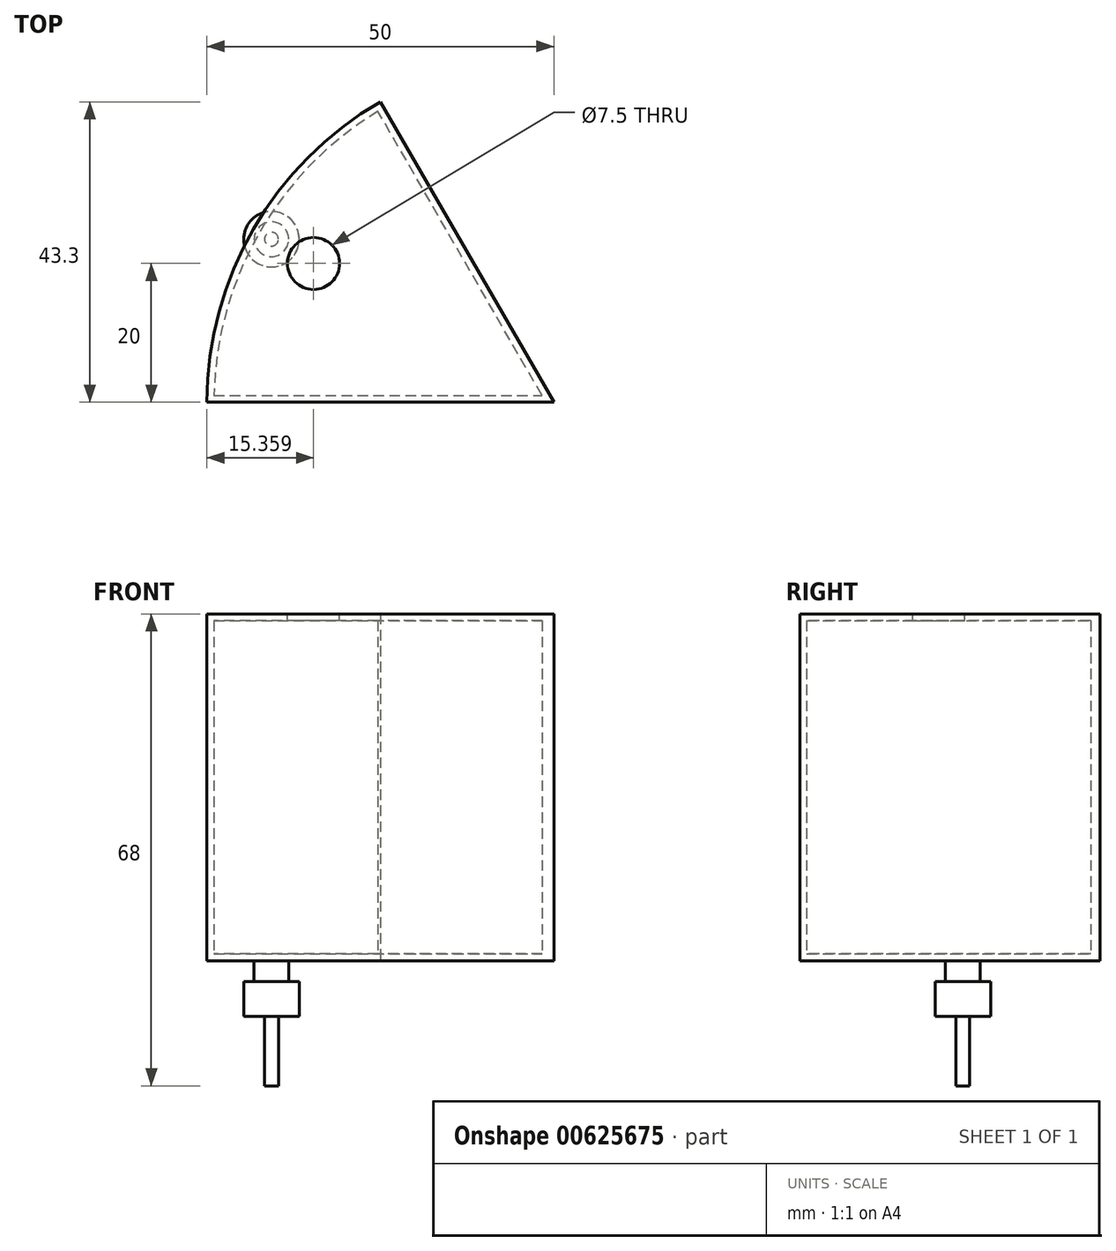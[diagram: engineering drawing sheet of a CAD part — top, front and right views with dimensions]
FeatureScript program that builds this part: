
annotation { "Feature Type Name" : "Feature", "Feature Type Description" : "" }
export const myFeature = defineFeature(function(context is Context, id is Id, definition is map)
    precondition{}
    {
        {
            var Q0;
            Q0=qCreatedBy(makeId("Top.planeOp"),FACE);
            var sketch = newSketch(context, id + "F0", { "sketchPlane" : qUnion([Q0])});
            skArc(sketch, "E0", {"start": v(-25, 43.3) * mm, "mid": v(-43.3, 25) * mm, "end": v(-50, 0) * mm});
            skLineSegment(sketch, "E1", {"start": v(-50, 0) * mm, "end": v(0, 0) * mm});
            skLineSegment(sketch, "E2", {"start": v(-25, 43.3) * mm, "end": v(0, 0) * mm});
            skSolve(sketch);
        }
        {
            var Q0;
            Q0=makeQuery(id+"F0.imprint","IMPRINT",FACE,{"disambiguationData":[TD([[makeQuery(id+"F0.imprint","IMPRINT",EDGE,{"derivedFrom":sQuery(id+"F0.wireOp",EDGE,"E0")}),1.0]])]});
            extrude(context, id + "F1", {"entities" : qUnion([Q0]), "depth" : 50 * mm, "offsetDistance" : 25 * mm});
        }
        {
            var Q0;
            Q0=qCreatedBy(makeId("Top.planeOp"),FACE);
            var sketch = newSketch(context, id + "F2", { "sketchPlane" : qUnion([Q0])});
            skArc(sketch, "E3", {"start": v(-25.36, 41.93) * mm, "mid": v(-42.44, 24.5) * mm, "end": v(-48.99, 1) * mm});
            skLineSegment(sketch, "E4", {"start": v(-48.99, 1) * mm, "end": v(-1.73, 1) * mm});
            skLineSegment(sketch, "E5", {"start": v(-1.73, 1) * mm, "end": v(-25.36, 41.93) * mm});
            skSolve(sketch);
        }
        {
            var Q0;
            Q0=makeQuery(id+"F2.imprint","IMPRINT",FACE,{"disambiguationData":[TD([[makeQuery(id+"F2.imprint","IMPRINT",EDGE,{"derivedFrom":sQuery(id+"F2.wireOp",EDGE,"E3")}),1.0]])]});
            extrude(context, id + "F3", {"entities" : qUnion([Q0]), "operationType" : NewBodyOperationType.REMOVE, "depth" : 49 * mm, "offsetDistance" : 25 * mm, "hasSecondDirection" : true, "secondDirectionOppositeDirection" : false, "secondDirectionDepth" : 1 * mm});
        }
        {
            var Q0;
            Q0=makeQuery(id+"F1.opExtrude","CAP_FACE",FACE,{"disambiguationData":[OSD([sQuery(id+"F0.wireOp",EDGE,"E0"),sQuery(id+"F0.wireOp",EDGE,"E1"),sQuery(id+"F0.wireOp",EDGE,"E2")])],"isStart":true});
            var sketch = newSketch(context, id + "F4", { "sketchPlane" : qUnion([Q0])});
            skCircle(sketch, "E6", {"center": v(-40.7, -23.5) * mm, "radius": 2.5 * mm});
            skSolve(sketch);
        }
        {
            var Q0;
            Q0=makeQuery(id+"F4.imprint","IMPRINT",FACE,{"disambiguationData":[TD([[makeQuery(id+"F4.imprint","IMPRINT",EDGE,{"derivedFrom":sQuery(id+"F4.wireOp",EDGE,"E6")}),1.0]])]});
            var Q1;
            Q1=sQuery(id+"F4.wireOp",EDGE,"E6");
            extrude(context, id + "F5", {"entities" : qUnion([Q0]), "operationType" : NewBodyOperationType.ADD, "surfaceEntities" : qUnion([Q1]), "depth" : 3 * mm, "offsetDistance" : 25 * mm});
        }
        {
            var Q0;
            Q0=makeQuery(id+"F5.opExtrude","CAP_FACE",FACE,{"disambiguationData":[OSD([sQuery(id+"F4.wireOp",EDGE,"E6")])],"isStart":false});
            var sketch = newSketch(context, id + "F6", { "sketchPlane" : qUnion([Q0])});
            skCircle(sketch, "E7", {"center": v(-40.7, -23.5) * mm, "radius": 4 * mm});
            skSolve(sketch);
        }
        {
            var Q0;
            Q0 = qSketchRegion(id + "F6", true);
            extrude(context, id + "F7", {"entities" : qUnion([Q0]), "operationType" : NewBodyOperationType.ADD, "depth" : 5 * mm, "offsetDistance" : 25 * mm});
        }
        {
            var Q0;
            Q0=makeQuery(id+"F7.opExtrude","CAP_FACE",FACE,{"disambiguationData":[OSD([sQuery(id+"F6.wireOp",EDGE,"E7")])],"isStart":false});
            var sketch = newSketch(context, id + "F8", { "sketchPlane" : qUnion([Q0])});
            skCircle(sketch, "E8", {"center": v(-40.7, -23.5) * mm, "radius": 1 * mm});
            skSolve(sketch);
        }
        {
            var Q0;
            Q0=makeQuery(id+"F8.imprint","IMPRINT",FACE,{"disambiguationData":[TD([[makeQuery(id+"F8.imprint","IMPRINT",EDGE,{"derivedFrom":sQuery(id+"F8.wireOp",EDGE,"E8")}),1.0]])]});
            extrude(context, id + "F9", {"entities" : qUnion([Q0]), "operationType" : NewBodyOperationType.ADD, "depth" : 10 * mm, "offsetDistance" : 25 * mm});
        }
        {
            var Q0;
            Q0=makeQuery(id+"F1.opExtrude","CAP_FACE",FACE,{"disambiguationData":[OSD([sQuery(id+"F0.wireOp",EDGE,"E0"),sQuery(id+"F0.wireOp",EDGE,"E1"),sQuery(id+"F0.wireOp",EDGE,"E2")])],"isStart":false});
            var sketch = newSketch(context, id + "F10", { "sketchPlane" : qUnion([Q0])});
            skCircle(sketch, "E9", {"center": v(-34.64, 20) * mm, "radius": 3.75 * mm});
            skSolve(sketch);
        }
        {
            var Q0;
            Q0 = qSketchRegion(id + "F10", true);
            extrude(context, id + "F11", {"entities" : qUnion([Q0]), "operationType" : NewBodyOperationType.REMOVE, "oppositeDirection" : true, "depth" : 2 * mm, "offsetDistance" : 25 * mm});
        }
    });
